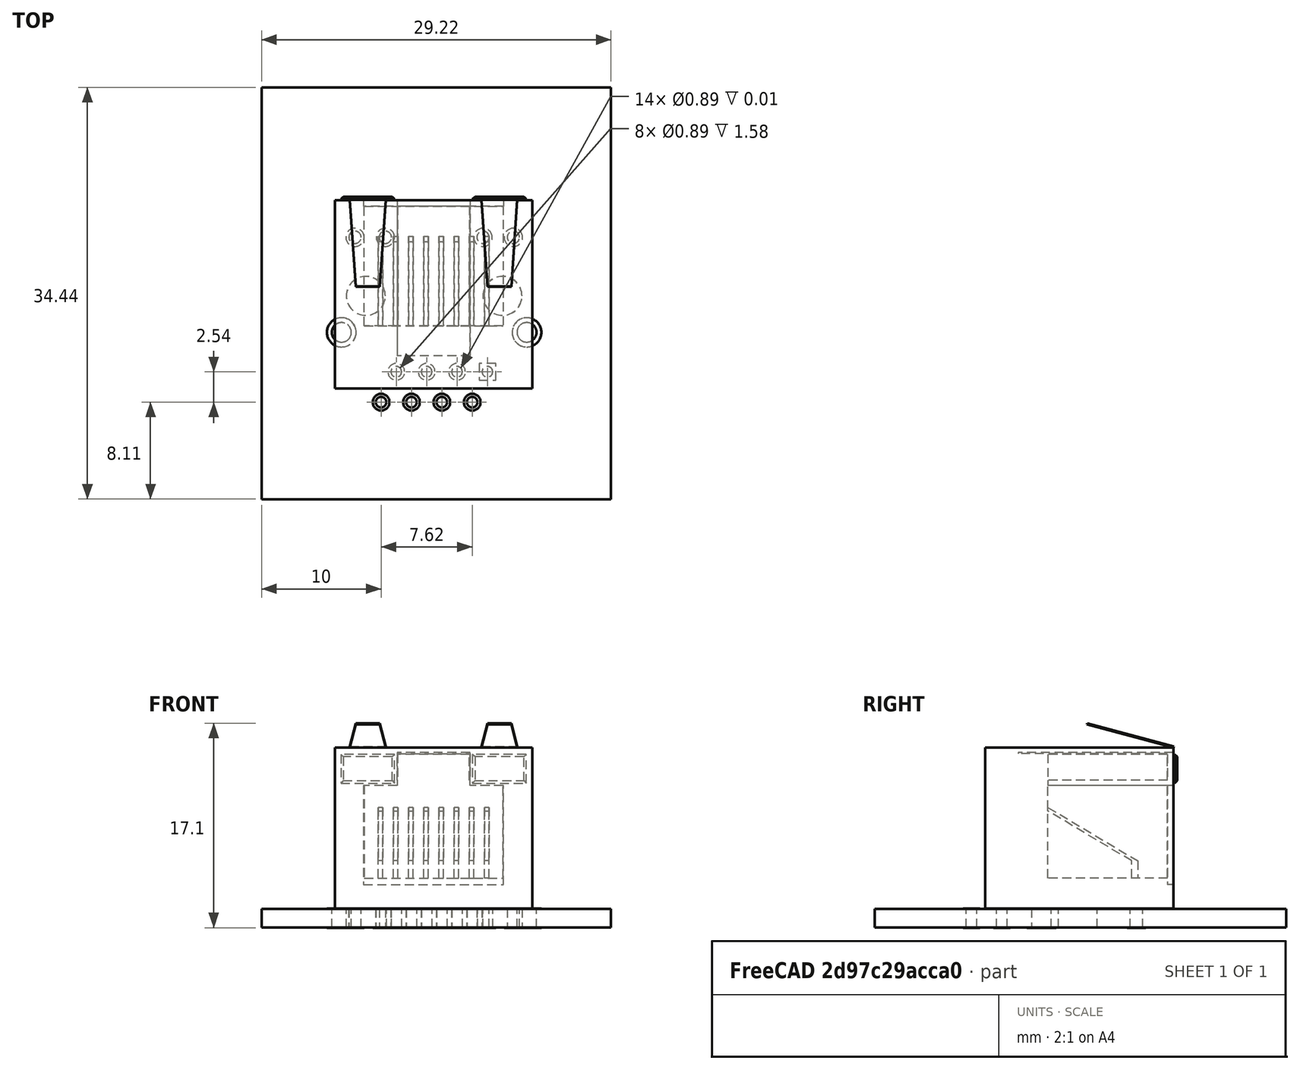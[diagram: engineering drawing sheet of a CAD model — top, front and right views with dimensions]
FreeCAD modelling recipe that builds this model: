
FCSTD DOCUMENT  (FreeCAD 0.19R18353 (Git))
Label: HANRUN_HR911105A
License: All rights reserved
LicenseURL: http://en.wikipedia.org/wiki/All_rights_reserved
objects: Part::FeaturePython×5, App::DocumentObjectGroup×1, Part::Feature×1, Part::Box×1, Part::Cut×1
note: 8 computed .brp shape members not serialized (recipe doc carries the construction recipe); baked Part::Feature solids carry a one-line shape summary decoded from their .brp

FEATURE [Part::FeaturePython] Filk_lines  label="FrontSilk"  # a2plus imported part (geometry in sourceFile) (typed FeaturePython)
  fixedPosition = true
FEATURE [Part::FeaturePython] TopPads  # a2plus imported part (geometry in sourceFile) (typed FeaturePython)
  fixedPosition = true
FEATURE [Part::FeaturePython] BotPads  # a2plus imported part (geometry in sourceFile) (typed FeaturePython)
  fixedPosition = true
FEATURE [Part::FeaturePython] THPs  label="PTHs"  # a2plus imported part (geometry in sourceFile) (typed FeaturePython)
  fixedPosition = true
FEATURE [Part::FeaturePython] newPCB  label="Pcb"  # a2plus imported part (geometry in sourceFile) (typed FeaturePython)
  fixedPosition = true
FEATURE [App::DocumentObjectGroup] HANRUN_HR911105A_fp
  Group = -> [Filk_lines,TopPads,BotPads,THPs,newPCB]
FEATURE [Part::Feature] Shape
  shape: bbox 16.51 x 16.05 x 18.68 mm, 163 faces, 3 solids (baked)
FEATURE [Part::Box] Box  label="Cube"
  AttacherType = Attacher::AttachEngine3D
  Height = 10
  Length = 20
  Placement = pos=(-10,-10,-10) rot=(0,0,1;0rad)
  Width = 20
FEATURE [Part::Cut] Cut
  Base = -> Shape
  Tool = -> Box
